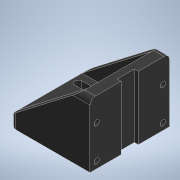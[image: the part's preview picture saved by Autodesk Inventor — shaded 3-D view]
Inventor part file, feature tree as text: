
AUTODESK INVENTOR PART (.ipt)
format: ipt  version: 2022.2 (Build 262287010, 287A)  size: 202,752 bytes
history: native  units: mm
features: sketch x7, extrude x6, mirror x2, hole x1, fillet x1
ambient origin geometry x8: Origin, YZ Plane, XZ Plane, XY Plane, X Axis, Y Axis, Z Axis, Center Point
bodies: Volumenkörper1 (feature_tree)
feature tree (17):
  extrude  "Extrusion1"  Depth=60.0mm
  extrude  "Extrusion2"  Depth=8.0mm
  hole  "Bohrung1"  [1 undecoded]
  extrude  "Extrusion3"  Depth=4.0mm
  extrude  "Extrusion4"  Depth=4.0mm
  mirror  "Spiegeln1"
  extrude  "Extrusion5"  Depth=7.0mm TaperAngle=0.0deg
  extrude  "Extrusion6"  Depth=6.0mm TaperAngle=0.0deg
  mirror  "Spiegeln2"
  fillet  "Rundung1"  Radius=25.0mm
  sketch  "Skizze1"  dims[d0=60.0mm d1=60.0mm]
  sketch  "Skizze2"  dims[d2=8.0mm d3=0.0mm d4=8.0mm]
  sketch  "Skizze3"  dims[d5=40.0mm d6=0.0mm d7=25.0mm]
  sketch  "Skizze4"  dims[d8=25.0mm d9=4.0mm]
  sketch  "Skizze5"  dims[d10=3.4mm d11=6.0mm d12=6.5mm d13=3.4mm d14=14.3117mm d15=8.0mm d16=20.594885mm d17=4.0mm]
  sketch  "Skizze6"  dims[d18=50.0mm d20=7.0mm d21=0.0mm]
  sketch  "Skizze7"  dims[d22=5.0mm d23=6.0mm d24=0.0mm d25=25.0mm d26=3.0mm d27=13.0mm d28=0.0mm d29=0.0mm d30=5.5mm d31=9.0mm d32=9.5mm d33=0.0mm d34=0.0mm d35=4.0mm]
note: 1 required parameter value undecoded (feature->parameter linkage not recoverable at this tier; creation-order binding heuristic only, values carry confidence <= 0.55)
